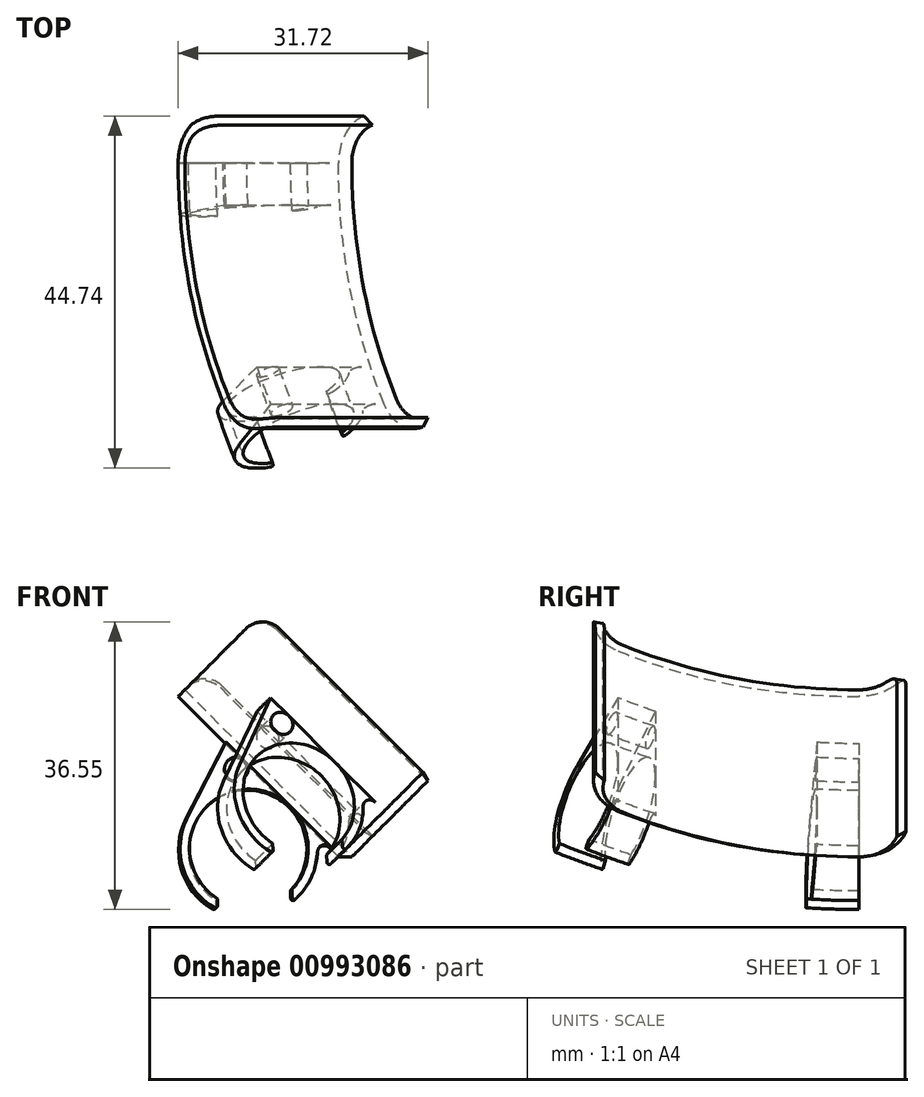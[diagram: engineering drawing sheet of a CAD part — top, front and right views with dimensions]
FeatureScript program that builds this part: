
annotation { "Feature Type Name" : "Feature", "Feature Type Description" : "" }
export const myFeature = defineFeature(function(context is Context, id is Id, definition is map)
    precondition{}
    {
        {
            var Q0;
            Q0=qCreatedBy(makeId("Front.planeOp"),FACE);
            var sketch = newSketch(context, id + "F0", { "sketchPlane" : qUnion([Q0])});
            skArc(sketch, "E0", {"start": v(6, -6.36) * mm, "mid": v(7.95, -3.66) * mm, "end": v(8.74, -0.43) * mm});
            skLineSegment(sketch, "E1", {"start": v(6.19, 6.19) * mm, "end": v(-7.95, 20.33) * mm});
            skArc(sketch, "E2.0", {"start": v(5.5, -5.17) * mm, "mid": v(-0.97, 7.49) * mm, "end": v(-4, -6.4) * mm});
            skLineSegment(sketch, "E3", {"start": v(5.5, -6.15) * mm, "end": v(5.5, -5.17) * mm});
            skLineSegment(sketch, "E4", {"start": v(-4, -7.27) * mm, "end": v(-4, -6.4) * mm});
            skLineSegment(sketch, "E5", {"start": v(6.19, 6.19) * mm, "end": v(13.26, -0.88) * mm});
            skLineSegment(sketch, "E6", {"start": v(-8.8, 19.48) * mm, "end": v(1.38, 9.3) * mm});
            skLineSegment(sketch, "E7", {"start": v(11.56, -0.88) * mm, "end": v(13.26, -0.88) * mm});
            skLineSegment(sketch, "E8", {"start": v(-8.8, 19.48) * mm, "end": v(-7.95, 20.33) * mm});
            skArc(sketch, "E9.trimOffspring", {"start": v(-7.77, 4.02) * mm, "mid": v(-8.4, -2.42) * mm, "end": v(-4.45, -7.53) * mm});
            skLineSegment(sketch, "E10.trimOffspring", {"start": v(10.45, 0.23) * mm, "end": v(11.56, -0.88) * mm});
            skPoint(sketch, "E11.visualSharp", {"position": v(2.21, 8.47) * mm});
            skPoint(sketch, "E12.visualSharp", {"position": v(8.47, 2.21) * mm});
            skArc(sketch, "E12.filletArc", {"start": v(10.45, 0.23) * mm, "mid": v(9.38, 0.46) * mm, "end": v(8.74, -0.43) * mm});
            skLineSegment(sketch, "E13", {"start": v(1.38, 9.3) * mm, "end": v(10.45, 0.23) * mm});
            skLineSegment(sketch, "E14", {"start": v(0.9, 18.55) * mm, "end": v(12.26, 7.19) * mm, "construction": true});
            skLineSegment(sketch, "E15", {"start": v(34.7, 62.53) * mm, "end": v(52.3, 44.93) * mm, "construction": true});
            skLineSegment(sketch, "E16", {"start": v(-2.85, 13.53) * mm, "end": v(-7.77, 4.02) * mm});
            skCircle(sketch, "E17", {"center": v(-1.57, 10.13) * mm, "radius": 1.5 * mm});
            skPoint(sketch, "E18.visualSharp", {"position": v(-4, -7.78) * mm});
            skArc(sketch, "E18.filletArc", {"start": v(-4.45, -7.53) * mm, "mid": v(-4.15, -7.53) * mm, "end": v(-4, -7.27) * mm});
            skPoint(sketch, "E19.visualSharp", {"position": v(5.5, -6.8) * mm});
            skArc(sketch, "E19.filletArc", {"start": v(5.5, -6.15) * mm, "mid": v(5.68, -6.42) * mm, "end": v(6, -6.36) * mm});
            skPoint(sketch, "E20.orphan", {"position": v(-9.85, 0) * mm});
            skSolve(sketch);
        }
        {
            var Q0;
            Q0=makeQuery(id+"F0.imprint","IMPRINT",FACE,{"disambiguationData":[TD([[makeQuery(id+"F0.imprint","IMPRINT",EDGE,{"derivedFrom":sQuery(id+"F0.wireOp",EDGE,"E1")}),1.0]])]});
            var Q1;
            Q1=sQuery(id+"F0.wireOp",EDGE,"E14");
            revolve(context, id + "F1", {"surfaceOperationType" : NewSurfaceOperationType.NEW, "entities" : qUnion([Q0]), "axis" : qUnion([Q1]), "revolveType" : RevolveType.ONE_DIRECTION, "angle" : 75 * degree});
        }
        {
            var Q0;
            Q0=makeQuery(id+"F0.imprint","IMPRINT",FACE,{"disambiguationData":[TD([[makeQuery(id+"F0.imprint","IMPRINT",EDGE,{"derivedFrom":sQuery(id+"F0.wireOp",EDGE,"E1")}),1.0]])]});
            var Q1;
            Q1=sQuery(id+"F0.wireOp",EDGE,"E15");
            revolve(context, id + "F2", {"surfaceOperationType" : NewSurfaceOperationType.NEW, "entities" : qUnion([Q0]), "axis" : qUnion([Q1]), "revolveType" : RevolveType.ONE_DIRECTION, "oppositeDirection" : true, "angle" : 15 * degree});
        }
        {
            var Q0;
            Q0=makeQuery(id+"F0.imprint","IMPRINT",FACE,{"disambiguationData":[TD([[makeQuery(id+"F0.imprint","IMPRINT",EDGE,{"derivedFrom":sQuery(id+"F0.wireOp",EDGE,"E0")}),1.0]])]});
            var Q1;
            Q1=sQuery(id+"F0.wireOp",EDGE,"E15");
            revolve(context, id + "F3", {"operationType" : NewBodyOperationType.ADD, "surfaceOperationType" : NewSurfaceOperationType.NEW, "entities" : qUnion([Q0]), "axis" : qUnion([Q1]), "revolveType" : RevolveType.ONE_DIRECTION, "oppositeDirection" : true, "angle" : 5 * degree});
        }
        {
            var Q0;
            {var subQ5=sQuery(id+"F0.wireOp",EDGE,"E4");Q0=makeQuery(id+"F0.imprint","IMPRINT",FACE,{"disambiguationData":[TD([[makeQuery(id+"F0.imprint","IMPRINT",EDGE,{"derivedFrom":subQ5}),1.0]])]});}
            var Q1;
            Q1=makeQuery(id+"F0.imprint","IMPRINT",FACE,{"disambiguationData":[TD([[makeQuery(id+"F0.imprint","IMPRINT",EDGE,{"derivedFrom":sQuery(id+"F0.wireOp",EDGE,"E17")}),1.0]])]});
            var Q2;
            Q2=sQuery(id+"F0.wireOp",EDGE,"E15");
            revolve(context, id + "F4", {"operationType" : NewBodyOperationType.ADD, "surfaceOperationType" : NewSurfaceOperationType.NEW, "entities" : qUnion([Q0, Q1]), "axis" : qUnion([Q2]), "revolveType" : RevolveType.ONE_DIRECTION, "oppositeDirection" : true, "angle" : 5 * degree});
        }
        {
            var Q0;
            Q0=makeQuery(id+"F0.imprint","IMPRINT",FACE,{"disambiguationData":[TD([[makeQuery(id+"F0.imprint","IMPRINT",EDGE,{"derivedFrom":sQuery(id+"F0.wireOp",EDGE,"E17")}),1.0]])]});
            var Q1;
            Q1=sQuery(id+"F0.wireOp",EDGE,"E15");
            revolve(context, id + "F5", {"operationType" : NewBodyOperationType.REMOVE, "surfaceOperationType" : NewSurfaceOperationType.NEW, "entities" : qUnion([Q0]), "axis" : qUnion([Q1]), "revolveType" : RevolveType.ONE_DIRECTION, "oppositeDirection" : true, "angle" : 10 * degree});
        }
        {
            var Q0;
            Q0=makeQuery(id+"F1.opRevolve","CAP_EDGE",EDGE,{"disambiguationData":[OSD([sQuery(id+"F0.wireOp",EDGE,"E8")])],"isStart":false});
            fillet(context, id + "F6", {"entities" : qUnion([Q0]), "radius" : 3 * mm, "tangentPropagation" : true, "allowEdgeOverflow" : false});
        }
        {
            var Q0;
            Q0=makeQuery(id+"F1.opRevolve","SWEPT_BODY",BODY,{"disambiguationData":[OSD([sQuery(id+"F0.wireOp",EDGE,"E1"),sQuery(id+"F0.wireOp",EDGE,"E5"),sQuery(id+"F0.wireOp",EDGE,"E6"),sQuery(id+"F0.wireOp",EDGE,"E7"),sQuery(id+"F0.wireOp",EDGE,"E8"),sQuery(id+"F0.wireOp",EDGE,"E10.trimOffspring"),sQuery(id+"F0.wireOp",EDGE,"E13")])]});
            var Q1;
            Q1=makeQuery(id+"F2.opRevolve","CAP_FACE",FACE,{"disambiguationData":[OSD([sQuery(id+"F0.wireOp",EDGE,"E1"),sQuery(id+"F0.wireOp",EDGE,"E5"),sQuery(id+"F0.wireOp",EDGE,"E6"),sQuery(id+"F0.wireOp",EDGE,"E7"),sQuery(id+"F0.wireOp",EDGE,"E8"),sQuery(id+"F0.wireOp",EDGE,"E10.trimOffspring"),sQuery(id+"F0.wireOp",EDGE,"E13")])],"isStart":false});
            mirror(context, id + "F7", {"operationType" : NewBodyOperationType.ADD, "entities" : qUnion([Q0]), "mirrorPlane" : qUnion([Q1])});
        }
    });
